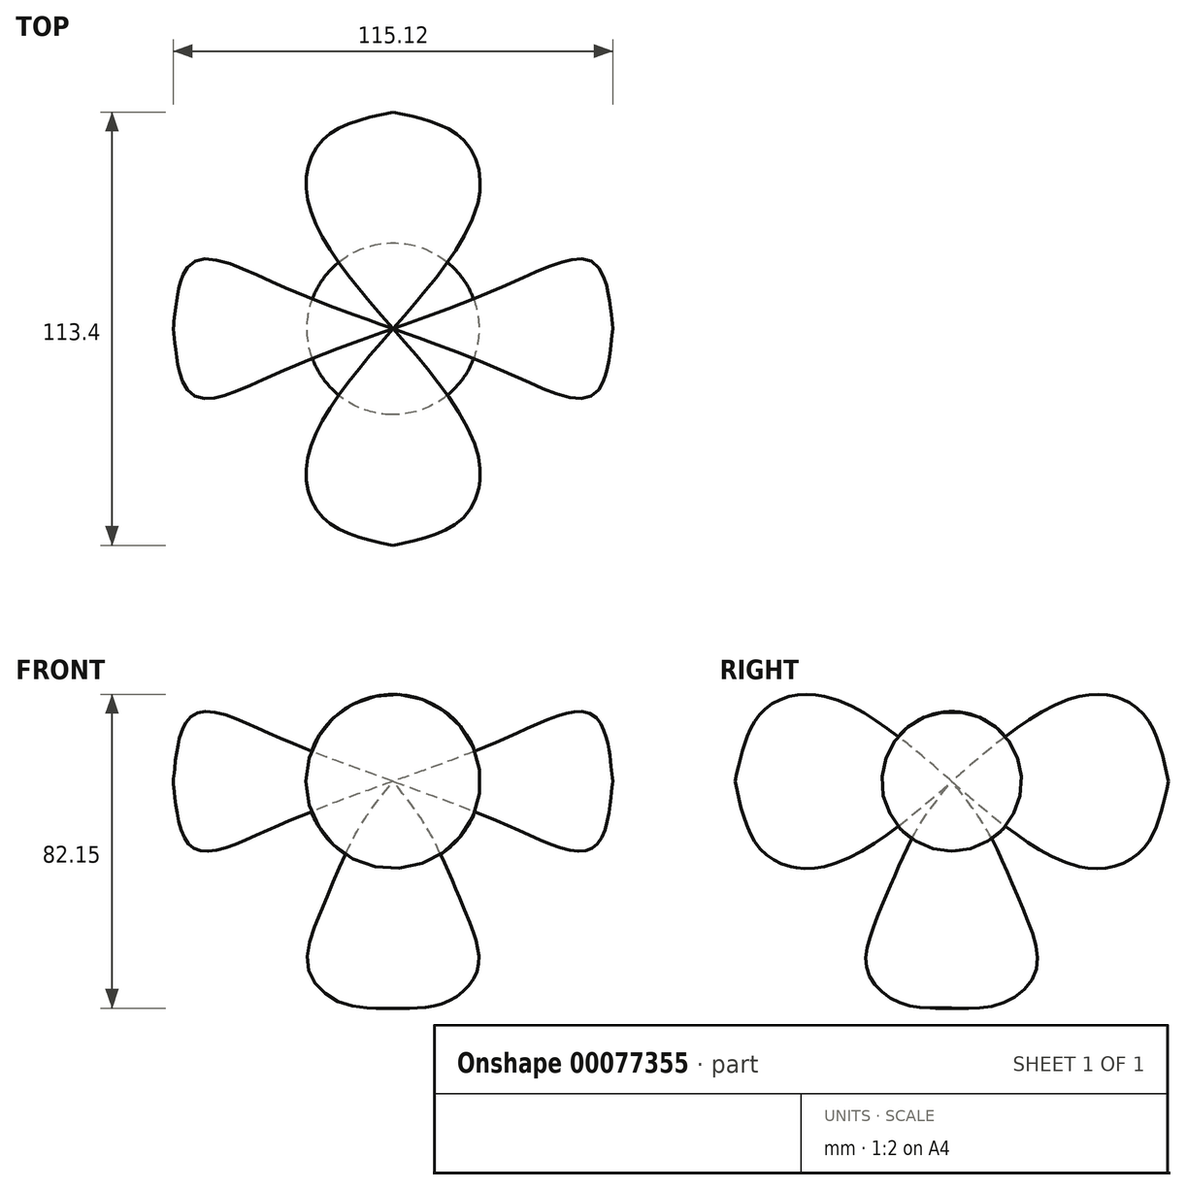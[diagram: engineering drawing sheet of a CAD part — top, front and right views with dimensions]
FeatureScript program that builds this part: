
annotation { "Feature Type Name" : "Feature", "Feature Type Description" : "" }
export const myFeature = defineFeature(function(context is Context, id is Id, definition is map)
    precondition{}
    {
        {
            var Q0;
            Q0=qCreatedBy(makeId("Right.planeOp"),FACE);
            var sketch = newSketch(context, id + "F0", { "sketchPlane" : qUnion([Q0])});
            skLineSegment(sketch, "E0", {"start": v(0, 59.25) * mm, "end": v(0, -59.25) * mm});
            skFitSpline(sketch, "E1", {"points": [v(0, 59.25) * mm, v(-13.7, 57.9) * mm, v(-22.15, 49.28) * mm, v(-19.78, 36.26) * mm, v(-13.86, 22.23) * mm, v(-8.11, 10.9) * mm, v(0, 0) * mm], "startDerivative": vector(-84.22, 3.12) * mm, "endDerivative": vector(51.77, -64.26) * mm});
            skFitSpline(sketch, "E2.MirrorCS", {"points": [v(0, -59.25) * mm, v(-13.7, -57.9) * mm, v(-22.15, -49.28) * mm, v(-19.78, -36.26) * mm, v(-13.86, -22.23) * mm, v(-8.11, -10.9) * mm, v(0, 0) * mm], "startDerivative": vector(-84.22, -3.12) * mm, "endDerivative": vector(51.77, 64.26) * mm});
            skFitSpline(sketch, "E3.MirrorCS", {"points": [v(0, 59.25) * mm, v(-13.7, 57.9) * mm, v(-22.15, 49.28) * mm, v(-19.78, 36.26) * mm, v(-13.86, 22.23) * mm, v(-8.11, 10.9) * mm, v(0, 0) * mm], "startDerivative": vector(-84.22, 3.12) * mm, "endDerivative": vector(51.77, -64.26) * mm});
            skSolve(sketch);
        }
        {
            var Q0;
            {var subQ0=sQuery(id+"F0.wireOp",EDGE,"E0");var subQ1=sQuery(id+"F0.wireOp",EDGE,"fa46a965-9c77-4637-98a4-c139bedc7d95");var subQ2=makeQuery(id+"F0.imprint","INTERSECT",VERTEX,{"derivedFrom":[subQ1,subQ0]});Q0=makeQuery(id+"F0.imprint","IMPRINT",FACE,{"disambiguationData":[TD([[makeQuery(id+"F0.imprint","IMPRINT",EDGE,{"disambiguationData":[TD([[subQ2,1.0]])],"derivedFrom":subQ1}),-1.0]])]});}
            var Q1;
            {var subQ0=sQuery(id+"F0.wireOp",EDGE,"7addd138-5621-4997-bab8-fed2c2be8bb4");var subQ1=makeQuery(id+"F0.imprint","INTERSECT",VERTEX,{"disambiguationData":[OD(0.0)],"derivedFrom":[sQuery(id+"F0.wireOp",EDGE,"fa46a965-9c77-4637-98a4-c139bedc7d95"),subQ0]});Q1=makeQuery(id+"F0.imprint","IMPRINT",FACE,{"disambiguationData":[TD([[makeQuery(id+"F0.imprint","IMPRINT",EDGE,{"disambiguationData":[TD([[subQ1,1.0]])],"derivedFrom":subQ0}),1.0]])]});}
            var Q2;
            {var subQ0=sQuery(id+"F0.wireOp",EDGE,"E3.MirrorCS");Q2=makeQuery(id+"F0.imprint","IMPRINT",FACE,{"disambiguationData":[TD([[makeQuery(id+"F0.imprint","IMPRINT",EDGE,{"derivedFrom":subQ0}),1.0]])]});}
            var Q3;
            {var subQ0=sQuery(id+"F0.wireOp",EDGE,"E2.MirrorCS");Q3=makeQuery(id+"F0.imprint","IMPRINT",FACE,{"disambiguationData":[TD([[makeQuery(id+"F0.imprint","IMPRINT",EDGE,{"derivedFrom":subQ0}),-1.0]])]});}
            var Q4;
            Q4=sQuery(id+"F0.wireOp",EDGE,"E0");
            revolve(context, id + "F1", {"entities" : qUnion([Q0, Q1, Q2, Q3]), "axis" : qUnion([Q4]), "revolveType" : RevolveType.FULL});
        }
        {
            var Q0;
            Q0=qCreatedBy(makeId("Front.planeOp"),FACE);
            var sketch = newSketch(context, id + "F2", { "sketchPlane" : qUnion([Q0])});
            skLineSegment(sketch, "E4", {"start": v(-57.56, 0) * mm, "end": v(57.73, 0) * mm});
            skFitSpline(sketch, "E5", {"points": [v(0, 0) * mm, v(-31.44, -12.17) * mm, v(-52.57, -17.24) * mm, v(-57.14, -3.55) * mm, v(-57.56, 0) * mm], "startDerivative": vector(-87.44, -31.18) * mm, "endDerivative": vector(-2.95, 22.18) * mm});
            skFitSpline(sketch, "E6.MirrorCS", {"points": [v(0, 0) * mm, v(31.44, -12.17) * mm, v(52.57, -17.24) * mm, v(57.14, -3.55) * mm, v(57.56, 0) * mm], "startDerivative": vector(87.44, -31.18) * mm, "endDerivative": vector(2.95, 22.18) * mm});
            skSolve(sketch);
        }
        {
            var Q0;
            {var subQ0=sQuery(id+"F2.wireOp",EDGE,"E5");Q0=makeQuery(id+"F2.imprint","IMPRINT",FACE,{"disambiguationData":[TD([[makeQuery(id+"F2.imprint","IMPRINT",EDGE,{"derivedFrom":subQ0}),-1.0]])]});}
            var Q1;
            {var subQ0=sQuery(id+"F2.wireOp",EDGE,"E6.MirrorCS");Q1=makeQuery(id+"F2.imprint","IMPRINT",FACE,{"disambiguationData":[TD([[makeQuery(id+"F2.imprint","IMPRINT",EDGE,{"derivedFrom":subQ0}),1.0]])]});}
            var Q2;
            Q2=sQuery(id+"F2.wireOp",EDGE,"E4");
            revolve(context, id + "F3", {"operationType" : NewBodyOperationType.ADD, "entities" : qUnion([Q0, Q1]), "axis" : qUnion([Q2]), "revolveType" : RevolveType.FULL});
        }
        {
            var Q0;
            Q0=qCreatedBy(makeId("Top.planeOp"),FACE);
            var sketch = newSketch(context, id + "F4", { "sketchPlane" : qUnion([Q0])});
            skLineSegment(sketch, "E7", {"start": v(0.02, -56.7) * mm, "end": v(0.02, 56.7) * mm});
            skFitSpline(sketch, "E8", {"points": [v(0, 0) * mm, v(-22.17, -32.96) * mm, v(-18.11, -49.7) * mm, v(0.02, -56.7) * mm], "startDerivative": vector(-69.86, -80.57) * mm, "endDerivative": vector(70.14, -14.7) * mm});
            skFitSpline(sketch, "E9.MirrorCS", {"points": [v(0, 0) * mm, v(-22.17, 32.96) * mm, v(-18.11, 49.7) * mm, v(0.02, 56.7) * mm], "startDerivative": vector(-69.86, 80.57) * mm, "endDerivative": vector(70.14, 14.7) * mm});
            skSolve(sketch);
        }
        {
            var Q0;
            Q0=makeQuery(id+"F4.imprint","IMPRINT",FACE,{"disambiguationData":[TD([[makeQuery(id+"F4.imprint","IMPRINT",EDGE,{"derivedFrom":sQuery(id+"F4.wireOp",EDGE,"E7")}),1.0]])]});
            var Q1;
            Q1=sQuery(id+"F4.wireOp",EDGE,"E7");
            revolve(context, id + "F5", {"entities" : qUnion([Q0]), "axis" : qUnion([Q1]), "revolveType" : RevolveType.FULL});
        }
    });
